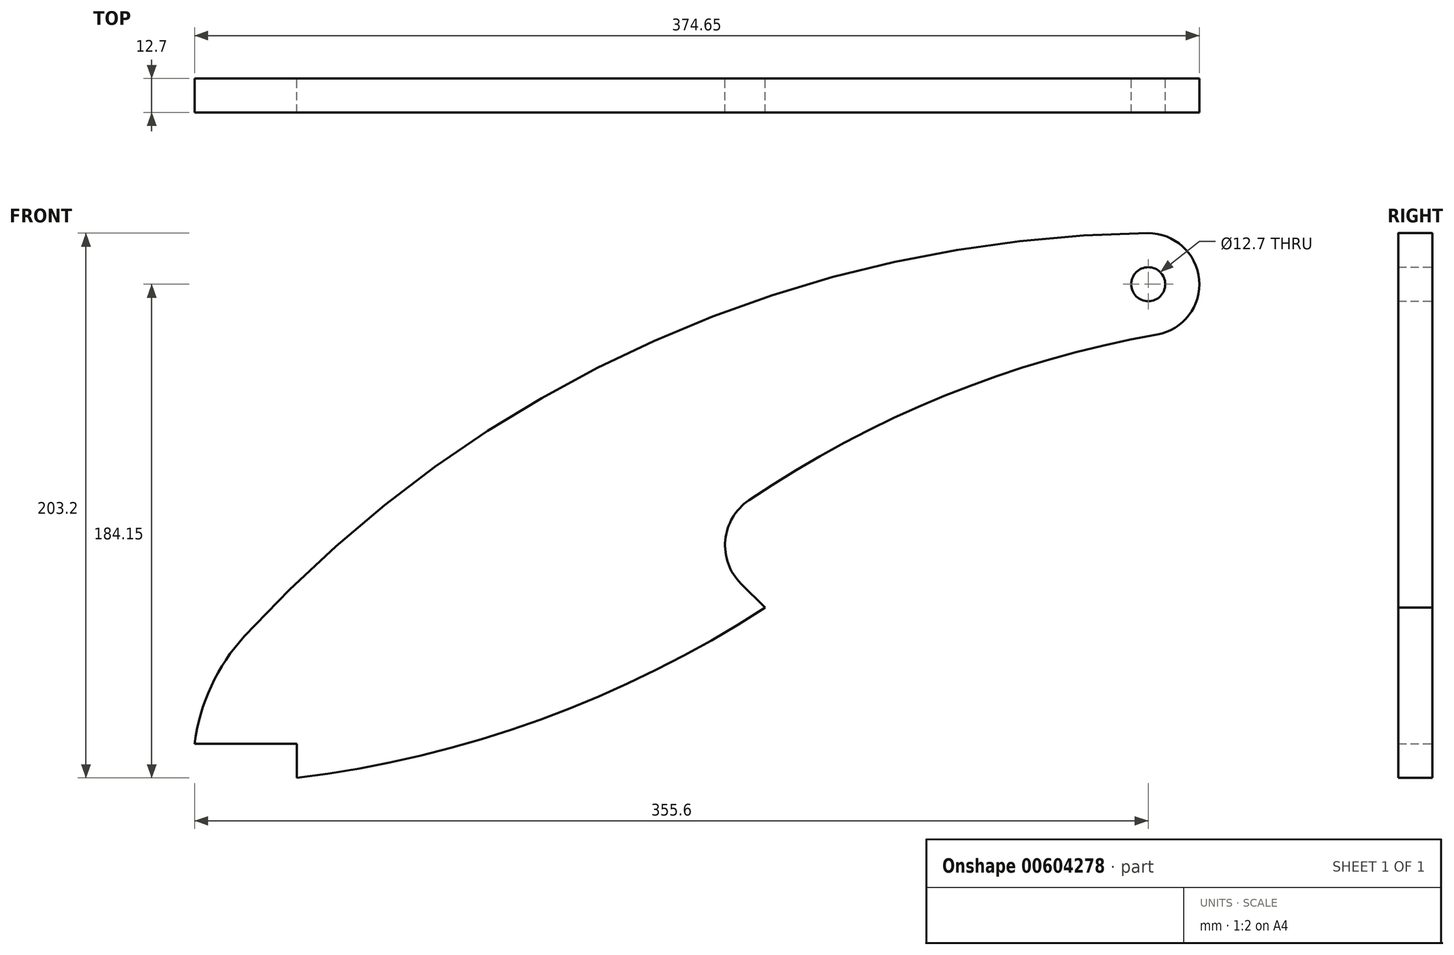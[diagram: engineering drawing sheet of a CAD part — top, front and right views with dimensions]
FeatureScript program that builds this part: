
annotation { "Feature Type Name" : "Feature", "Feature Type Description" : "" }
export const myFeature = defineFeature(function(context is Context, id is Id, definition is map)
    precondition{}
    {
        {
            var Q0;
            Q0=qCreatedBy(makeId("Front.planeOp"),FACE);
            var sketch = newSketch(context, id + "F0", { "sketchPlane" : qUnion([Q0])});
            skLineSegment(sketch, "E0", {"start": v(25.4, 25.4) * mm, "end": v(63.5, 25.4) * mm});
            skLineSegment(sketch, "E1", {"start": v(63.5, 25.4) * mm, "end": v(63.5, 12.7) * mm});
            skCircle(sketch, "E2", {"center": v(381, 196.85) * mm, "radius": 6.35 * mm});
            skCircle(sketch, "E3", {"center": v(381, 196.85) * mm, "radius": 19.05 * mm});
            skLineSegment(sketch, "E4", {"start": v(238.13, 76.2) * mm, "end": v(229.14, 85.18) * mm});
            skArc(sketch, "E5", {"start": v(63.5, 12.7) * mm, "mid": v(154.43, 34.5) * mm, "end": v(238.12, 76.2) * mm});
            skArc(sketch, "E6", {"start": v(232.11, 116.3) * mm, "mid": v(223.3, 101.44) * mm, "end": v(229.14, 85.18) * mm});
            skArc(sketch, "E7", {"start": v(384.34, 178.1) * mm, "mid": v(304.97, 155.2) * mm, "end": v(232.11, 116.3) * mm});
            skArc(sketch, "E8", {"start": v(44.03, 65.6) * mm, "mid": v(31.6, 46.95) * mm, "end": v(25.4, 25.4) * mm});
            skArc(sketch, "E9", {"start": v(380.8, 215.9) * mm, "mid": v(196.8, 175.73) * mm, "end": v(44.03, 65.6) * mm});
            skSolve(sketch);
        }
        {
            var Q0;
            Q0=makeQuery(id+"F0.imprint","IMPRINT",FACE,{"disambiguationData":[TD([[makeQuery(id+"F0.imprint","IMPRINT",EDGE,{"derivedFrom":sQuery(id+"F0.wireOp",EDGE,"E0")}),1.0]])]});
            var Q1;
            Q1=makeQuery(id+"F0.imprint","IMPRINT",FACE,{"disambiguationData":[TD([[makeQuery(id+"F0.imprint","IMPRINT",EDGE,{"derivedFrom":sQuery(id+"F0.wireOp",EDGE,"E2")}),-1.0]])]});
            extrude(context, id + "F1", {"entities" : qUnion([Q0, Q1]), "depth" : 12.7 * mm, "offsetDistance" : 25.4 * mm});
        }
    });
